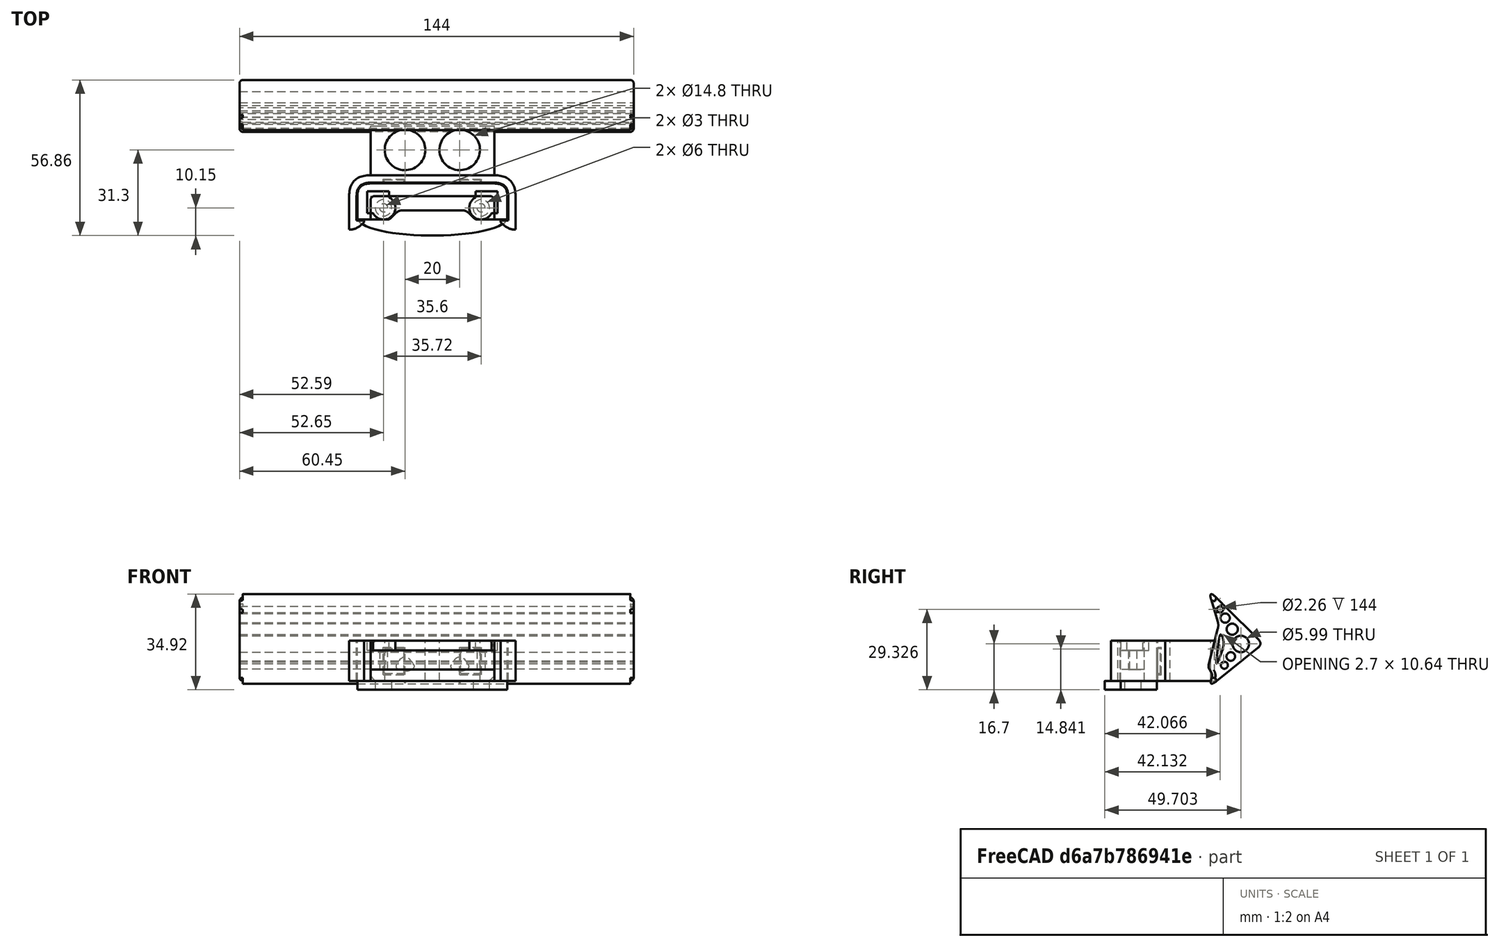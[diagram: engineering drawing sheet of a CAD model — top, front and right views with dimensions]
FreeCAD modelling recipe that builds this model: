
FCSTD DOCUMENT  (FreeCAD 0.19R0.19.2)
Label: 039
License: All rights reserved
LicenseURL: http://en.wikipedia.org/wiki/All_rights_reserved
objects: Sketcher::SketchObject×6, Part::Extrusion×6, Part::Box×5, Part::Cylinder×4, Part::Fillet×3, Part::MultiFuse×2, Part::Cut×2
note: 28 computed .brp shape members not serialized (recipe doc carries the construction recipe); baked Part::Feature solids carry a one-line shape summary decoded from their .brp

FEATURE [Sketcher::SketchObject] Sketch  label="attatchmentPiece"
  FullyConstrained = true
  sketch-geometry (20):
    g0: Circle CenterX=16.25 CenterY=0 CenterZ=0 NormalX=0 NormalY=0 NormalZ=1 AngleXU=0 Radius=1.5
    g1: LineSegment StartX=21.05 StartY=0 StartZ=0 EndX=21.05 EndY=-1 EndZ=0
    g2: LineSegment StartX=21.05 StartY=-1 StartZ=0 EndX=21.05 EndY=-4.3 EndZ=0
    g3: LineSegment StartX=-24.15 StartY=4.3 StartZ=0 EndX=21.05 EndY=4.3 EndZ=0
    g4: LineSegment StartX=21.05 StartY=0 StartZ=0 EndX=21.05 EndY=4.3 EndZ=0
    g5-g8: Circle x4 (B-spline internal-alignment scaffolding for g9; pole/knot coordinates omitted)
    g9: BSplineCurve PolesCount=4 KnotsCount=2 Degree=3 IsPeriodic=0
    g10: GeomPoint X=10.05 Y=-1 Z=0
    g11: GeomPoint X=14.55 Y=-4.3 Z=0
    g12: LineSegment StartX=10.05 StartY=-1 StartZ=0 EndX=-10.05 EndY=-1 EndZ=0
    g13: LineSegment StartX=14.55 StartY=-4.3 StartZ=0 EndX=21.05 EndY=-4.3 EndZ=0
    g14: LineSegment StartX=-24.15 StartY=4.3 StartZ=0 EndX=-24.15 EndY=-4.3 EndZ=0
    g15: LineSegment StartX=-13.15 StartY=-1 StartZ=0 EndX=-10.05 EndY=-1 EndZ=0
    g16: LineSegment StartX=-24.15 StartY=-4.3 StartZ=0 EndX=-19.35 EndY=-4.3 EndZ=0
    g17: Circle CenterX=-19.35 CenterY=0 CenterZ=0 NormalX=0 NormalY=0 NormalZ=1 AngleXU=0 Radius=1.5
    g18: LineSegment StartX=-19.35 StartY=-4.3 StartZ=0 EndX=-17.65 EndY=-4.3 EndZ=0
    g19: BSplineCurve PolesCount=4 KnotsCount=2 Degree=3 IsPeriodic=0
  constraints (41):
    c: Block(g0)
    c: Vertical(g1)
    c: Coincident(g2,g1)
    c: Vertical(g2)
    c: Block(g1)
    c: Horizontal(g3)
    c: Vertical(g4)
    c: Coincident(g4,g3)
    c: Block(g3)
    c: Block(g4)
    c: Weight(g5) = 1
    c: Equal(g5,g6)
    c: Equal(g5,g7)
    c: Equal(g5,g8)
    c: InternalAlignment(g5-g8 -> g9) x4
    c: InternalAlignment(g10,g9)
    c: InternalAlignment(g11,g9)
    c: Block(g9)
    c: Coincident(g12,g9)
    c: Horizontal(g12)
    c: Coincident(g13,g9)
    c: Coincident(g13,g2)
    c: Horizontal(g13)
    c: Distance(g3) = 45.2
    c: Coincident(g14,g3)
    c: Vertical(g14)
    c: Horizontal(g15)
    c: Distance(g15) = 3.1
    c: Block(g17)
    c: Horizontal(g16)
    c: Block(g19)
    c: Coincident(g18,g16)
    c: Coincident(g18,g19)
    c: Horizontal(g18)
    c: Block(g18)
    c: Coincident(g19,g15)
    c: Block(g16)
    c: Block(g12)
    c: Block(g14)
    c: Distance(g16) = 4.8
    c: Distance(g18) = 1.7
FEATURE [Part::Extrusion] Extrude  label="attatchmentPiece001"
  Base = -> Sketch
  Dir = (0,0,1)
  DirMode = 2
  FaceMakerClass = Part::FaceMakerBullseye
  LengthFwd = 7
  LengthRev = 0
  Solid = true
  Symmetric = false
FEATURE [Sketcher::SketchObject] Sketch001  label="attatchmentPieceSurround"
  FullyConstrained = true
  sketch-geometry (18):
    g0: LineSegment StartX=25.85 StartY=-4.3 StartZ=0 EndX=21.05 EndY=-4.3 EndZ=0
    g1: LineSegment StartX=25.85 StartY=-4.3 StartZ=0 EndX=25.85 EndY=4.3 EndZ=0
    g2: LineSegment StartX=-21.05 StartY=8.9 StartZ=0 EndX=21.05 EndY=8.9 EndZ=0
    g3: Circle CenterX=21.05 CenterY=8.9 CenterZ=0 NormalX=0 NormalY=0 NormalZ=1 AngleXU=0 Radius=1
    g4: Circle CenterX=25.85 CenterY=8.9 CenterZ=0 NormalX=0 NormalY=0 NormalZ=1 AngleXU=0 Radius=1
    g5: Circle CenterX=25.85 CenterY=4.3 CenterZ=0 NormalX=0 NormalY=0 NormalZ=1 AngleXU=0 Radius=1
    g6: BSplineCurve PolesCount=3 KnotsCount=2 Degree=2 IsPeriodic=0
    g7: GeomPoint X=21.05 Y=8.9 Z=0
    g8: GeomPoint X=25.85 Y=4.3 Z=0
    g9: ArcOfCircle CenterX=19.45 CenterY=2.7 CenterZ=0 NormalX=0 NormalY=0 NormalZ=1 AngleXU=0 Radius=1.6 StartAngle=0 EndAngle=1.5708
    g10: LineSegment StartX=21.05 StartY=2.7 StartZ=0 EndX=21.05 EndY=-4.3 EndZ=0
    g11: BSplineCurve PolesCount=3 KnotsCount=2 Degree=2 IsPeriodic=0
    g12: LineSegment StartX=-28.95 StartY=-4.3 StartZ=0 EndX=-28.95 EndY=4.3 EndZ=0
    g13: LineSegment StartX=-24.15 StartY=-4.3 StartZ=0 EndX=-28.95 EndY=-4.3 EndZ=0
    g14: LineSegment StartX=-24.15 StartY=2.7 StartZ=0 EndX=-24.15 EndY=-4.3 EndZ=0
    g15: ArcOfCircle CenterX=-22.55 CenterY=2.7 CenterZ=0 NormalX=0 NormalY=0 NormalZ=1 AngleXU=0 Radius=1.6 StartAngle=1.5708 EndAngle=3.14159
    g16: LineSegment StartX=-24.15 StartY=8.9 StartZ=0 EndX=-21.05 EndY=8.9 EndZ=0
    g17: LineSegment StartX=-22.55 StartY=4.3 StartZ=0 EndX=19.45 EndY=4.3 EndZ=0
  constraints (38):
    c: Horizontal(g0)
    c: Vertical(g1)
    c: Coincident(g1,g0)
    c: Horizontal(g2)
    c: Distance(g2) = 42.1
    c: Block(g2)
    c: Coincident(g6,g2)
    c: Weight(g3) = 1
    c: Equal(g3,g4)
    c: Equal(g3,g5)
    c: Coincident(g6,g1)
    c: InternalAlignment(g3,g6)
    c: InternalAlignment(g4,g6)
    c: InternalAlignment(g5,g6)
    c: InternalAlignment(g7,g6)
    c: InternalAlignment(g8,g6)
    c: Block(g0)
    c: Block(g6)
    c: Block(g9)
    c: Coincident(g10,g9)
    c: Coincident(g10,g0)
    c: Vertical(g10)
    c: Horizontal(g13)
    c: Coincident(g12,g13)
    c: Vertical(g12)
    c: Coincident(g11,g12)
    c: Block(g12)
    c: Block(g11)
    c: Block(g15)
    c: Coincident(g14,g15)
    c: Coincident(g14,g13)
    c: Vertical(g14)
    c: Coincident(g16,g11)
    c: Coincident(g16,g2)
    c: Horizontal(g16)
    c: Coincident(g17,g15)
    c: Coincident(g17,g9)
    c: Horizontal(g17)
FEATURE [Part::Extrusion] Extrude001  label="attatchmentPieceSurround001"
  Base = -> Sketch001
  Dir = (0,0,1)
  DirMode = 2
  FaceMakerClass = Part::FaceMakerBullseye
  LengthFwd = 14.7
  LengthRev = 0
  Placement = pos=(0,0,-4.1) rot=(0,0,1;0rad)
  Solid = true
  Symmetric = false
FEATURE [Sketcher::SketchObject] Sketch002  label="attatchmentPieceEndScrewHoleCaps"
  FullyConstrained = true
  sketch-geometry (10):
    g0: ArcOfCircle CenterX=16.25 CenterY=0 CenterZ=0 NormalX=0 NormalY=0 NormalZ=1 AngleXU=0 Radius=4.3 StartAngle=2.05456 EndAngle=5.79942
    g1: LineSegment StartX=14.25 StartY=3.80657 StartZ=0 EndX=14.25 EndY=6 EndZ=0
    g2: LineSegment StartX=20.0566 StartY=-2 StartZ=0 EndX=22.25 EndY=-2 EndZ=0
    g3: LineSegment StartX=22.25 StartY=-2 StartZ=0 EndX=22.25 EndY=6 EndZ=0
    g4: LineSegment StartX=14.25 StartY=6 StartZ=0 EndX=22.25 EndY=6 EndZ=0
    g5: LineSegment StartX=-25.35 StartY=-2 StartZ=0 EndX=-25.35 EndY=6 EndZ=0
    g6: LineSegment StartX=-25.35 StartY=-2 StartZ=0 EndX=-23.1566 EndY=-2 EndZ=0
    g7: LineSegment StartX=-17.35 StartY=6 StartZ=0 EndX=-25.35 EndY=6 EndZ=0
    g8: LineSegment StartX=-17.35 StartY=3.80657 StartZ=0 EndX=-17.35 EndY=6 EndZ=0
    g9: ArcOfCircle CenterX=-19.35 CenterY=0 CenterZ=0 NormalX=0 NormalY=0 NormalZ=1 AngleXU=0 Radius=4.3 StartAngle=3.62536 EndAngle=7.37022
  constraints (25):
    c: Block(g0)
    c: Vertical(g1)
    c: Horizontal(g2)
    c: Coincident(g3,g2)
    c: Vertical(g3)
    c: Coincident(g4,g1)
    c: Horizontal(g4)
    c: Coincident(g3,g4)
    c: Block(g4)
    c: Block(g3)
    c: Coincident(g0,g1)
    c: Coincident(g0,g2)
    c: Block(g1)
    c: Block(g9)
    c: Horizontal(g6)
    c: Vertical(g8)
    c: Coincident(g7,g8)
    c: Horizontal(g7)
    c: Coincident(g5,g6)
    c: Vertical(g5)
    c: Coincident(g5,g7)
    c: Block(g7)
    c: Block(g5)
    c: Coincident(g9,g6)
    c: Coincident(g9,g8)
FEATURE [Part::Extrusion] Extrude002  label="attatchmentPieceEndScrewHoleCaps001"
  Base = -> Sketch002
  Dir = (0,0,1)
  DirMode = 2
  FaceMakerClass = Part::FaceMakerBullseye
  LengthFwd = 3.6
  LengthRev = 0
  Placement = pos=(0,0,7) rot=(0,0,1;0rad)
  Solid = true
  Symmetric = false
FEATURE [Sketcher::SketchObject] Sketch003  label="mainBumpperPieceAttatchment"
  FullyConstrained = true
  sketch-geometry (42):
    g0: Circle CenterX=28.85 CenterY=4.3 CenterZ=0 NormalX=0 NormalY=0 NormalZ=1 AngleXU=0 Radius=1
    g1: Circle CenterX=28.85 CenterY=11.9 CenterZ=0 NormalX=0 NormalY=0 NormalZ=1 AngleXU=0 Radius=1
    g2: Circle CenterX=21.05 CenterY=11.9 CenterZ=0 NormalX=0 NormalY=0 NormalZ=1 AngleXU=0 Radius=1
    g3: BSplineCurve PolesCount=3 KnotsCount=2 Degree=2 IsPeriodic=0
    g4: GeomPoint X=28.85 Y=4.3 Z=0
    g5: GeomPoint X=21.05 Y=11.9 Z=0
    g6: LineSegment StartX=-21.05 StartY=11.9 StartZ=0 EndX=21.05 EndY=11.9 EndZ=0
    g7: LineSegment StartX=28.85 StartY=4.3 StartZ=0 EndX=28.85 EndY=-4.3 EndZ=0
    g8: Circle CenterX=21.05 CenterY=9.2 CenterZ=0 NormalX=0 NormalY=0 NormalZ=1 AngleXU=0 Radius=1
    g9: Circle CenterX=26.15 CenterY=9.2 CenterZ=0 NormalX=0 NormalY=0 NormalZ=1 AngleXU=0 Radius=1
    g10: Circle CenterX=26.15 CenterY=4.3 CenterZ=0 NormalX=0 NormalY=0 NormalZ=1 AngleXU=0 Radius=1
    g11: BSplineCurve PolesCount=3 KnotsCount=2 Degree=2 IsPeriodic=0
    g12: GeomPoint X=21.05 Y=9.2 Z=0
    g13: GeomPoint X=26.15 Y=4.3 Z=0
    g14: LineSegment StartX=-21.05 StartY=9.2 StartZ=0 EndX=21.05 EndY=9.2 EndZ=0
    g15: LineSegment StartX=26.15 StartY=-4.3 StartZ=0 EndX=26.15 EndY=4.3 EndZ=0
    g16: LineSegment StartX=26.15 StartY=-4.3 StartZ=0 EndX=26.15 EndY=-4.6 EndZ=0
    g17: LineSegment StartX=23.45 StartY=-4.6 StartZ=0 EndX=26.15 EndY=-4.6 EndZ=0
    g18: LineSegment StartX=28.85 StartY=-4.3 StartZ=0 EndX=28.85 EndY=-7.9 EndZ=0
    g19: LineSegment StartX=23.45 StartY=-4.6 StartZ=0 EndX=23.45 EndY=-5.3 EndZ=0
    g20: Circle CenterX=28.85 CenterY=-7.9 CenterZ=0 NormalX=0 NormalY=0 NormalZ=1 AngleXU=0 Radius=1
    g21: Circle CenterX=26.15 CenterY=-8.2 CenterZ=0 NormalX=0 NormalY=0 NormalZ=1 AngleXU=0 Radius=1
    g22: Circle CenterX=23.45 CenterY=-5.3 CenterZ=0 NormalX=0 NormalY=0 NormalZ=1 AngleXU=0 Radius=1
    g23: BSplineCurve PolesCount=3 KnotsCount=2 Degree=2 IsPeriodic=0
    g24: GeomPoint X=28.85 Y=-7.9 Z=0
    g25: GeomPoint X=23.45 Y=-5.3 Z=0
    g26: LineSegment StartX=-21.05 StartY=9.2 StartZ=0 EndX=-24.15 EndY=9.2 EndZ=0
    g27: BSplineCurve PolesCount=3 KnotsCount=2 Degree=2 IsPeriodic=0
    g28: LineSegment StartX=-29.25 StartY=-4.3 StartZ=0 EndX=-29.25 EndY=-4.6 EndZ=0
    g29: LineSegment StartX=-29.25 StartY=-4.6 StartZ=0 EndX=-26.55 EndY=-4.6 EndZ=0
    g30: LineSegment StartX=-31.95 StartY=-4.3 StartZ=0 EndX=-31.95 EndY=-7.9 EndZ=0
    g31: LineSegment StartX=-26.55 StartY=-4.6 StartZ=0 EndX=-26.55 EndY=-5.3 EndZ=0
    g32: Circle CenterX=-31.95 CenterY=-7.9 CenterZ=0 NormalX=0 NormalY=0 NormalZ=1 AngleXU=0 Radius=1
    g33: Circle CenterX=-29.25 CenterY=-8.2 CenterZ=0 NormalX=0 NormalY=0 NormalZ=1 AngleXU=0 Radius=1
    g34: Circle CenterX=-26.55 CenterY=-5.3 CenterZ=0 NormalX=0 NormalY=0 NormalZ=1 AngleXU=0 Radius=1
    g35: BSplineCurve PolesCount=3 KnotsCount=2 Degree=2 IsPeriodic=0
    g36: GeomPoint X=-31.95 Y=-7.9 Z=0
    g37: GeomPoint X=-26.55 Y=-5.3 Z=0
    g38: LineSegment StartX=-31.95 StartY=4.3 StartZ=0 EndX=-31.95 EndY=-4.3 EndZ=0
    g39: LineSegment StartX=-29.25 StartY=-4.3 StartZ=0 EndX=-29.25 EndY=4.3 EndZ=0
    g40: BSplineCurve PolesCount=3 KnotsCount=2 Degree=2 IsPeriodic=0
    g41: LineSegment StartX=-21.05 StartY=11.9 StartZ=0 EndX=-24.15 EndY=11.9 EndZ=0
  constraints (78):
    c: Weight(g0) = 1
    c: Equal(g0,g1)
    c: Equal(g0,g2)
    c: InternalAlignment(g0,g3)
    c: InternalAlignment(g1,g3)
    c: InternalAlignment(g2,g3)
    c: InternalAlignment(g4,g3)
    c: InternalAlignment(g5,g3)
    c: Block(g3)
    c: Horizontal(g6)
    c: Vertical(g7)
    c: Block(g7)
    c: Block(g6)
    c: Weight(g8) = 1
    c: Equal(g8,g9)
    c: Equal(g8,g10)
    c: InternalAlignment(g8,g11)
    c: InternalAlignment(g9,g11)
    c: InternalAlignment(g10,g11)
    c: InternalAlignment(g12,g11)
    c: InternalAlignment(g13,g11)
    c: Horizontal(g14)
    c: Vertical(g15)
    c: Block(g11)
    c: Block(g15)
    c: Block(g14)
    c: Coincident(g16,g15)
    c: Vertical(g16)
    c: Distance(g16) = 0.3
    c: Horizontal(g17)
    c: Coincident(g17,g16)
    c: Coincident(g18,g7)
    c: Vertical(g18)
    c: Distance(g18) = 3.6
    c: Vertical(g19)
    c: Coincident(g19,g17)
    c: Coincident(g23,g18)
    c: Weight(g20) = 1
    c: Equal(g20,g21)
    c: Equal(g20,g22)
    c: Coincident(g23,g19)
    c: InternalAlignment(g20,g23)
    c: InternalAlignment(g21,g23)
    c: InternalAlignment(g22,g23)
    c: InternalAlignment(g24,g23)
    c: InternalAlignment(g25,g23)
    c: Block(g23)
    c: Horizontal(g26)
    c: Distance(g26) = 3.1
    c: Block(g27)
    c: Vertical(g38)
    c: Block(g38)
    c: Vertical(g39)
    c: Block(g40)
    c: Block(g39)
    c: Vertical(g28)
    c: Coincident(g28,g39)
    c: Coincident(g29,g28)
    c: Horizontal(g29)
    c: Vertical(g30)
    c: Coincident(g30,g38)
    c: Coincident(g31,g29)
    c: Vertical(g31)
    c: Coincident(g35,g30)
    c: Equal(g32,g33)
    c: Equal(g32,g34)
    c: Coincident(g35,g31)
    c: InternalAlignment(g32,g35)
    c: InternalAlignment(g33,g35)
    c: InternalAlignment(g34,g35)
    c: InternalAlignment(g36,g35)
    c: InternalAlignment(g37,g35)
    c: Block(g35)
    c: Coincident(g40,g26)
    c: Block(g29)
    c: Horizontal(g41)
    c: Equal(g26,g41) = 3.1
    c: Coincident(g41,g6)
FEATURE [Part::Box] Box  label="bumpperExtension"
  AttacherType = Attacher::AttachEngine3D
  Height = 14.7
  Length = 45.2
  Placement = pos=(-24.15,11.9,-4.1) rot=(0,0,1;0rad)
  Width = 18
FEATURE [Sketcher::SketchObject] Sketch004  label="bumpperMain"
  FullyConstrained = true
  Placement = pos=(0,0,0) rot=(0.57735,0.57735,0.57735;2.0944rad)
  sketch-geometry (62):
    g0: Circle CenterX=-3.12329 CenterY=2.49901 CenterZ=0 NormalX=0 NormalY=0 NormalZ=1 AngleXU=0 Radius=1
    g1: Circle CenterX=0 CenterY=0 CenterZ=0 NormalX=0 NormalY=0 NormalZ=1 AngleXU=0 Radius=1
    g2: Circle CenterX=-1.35243 CenterY=3.60648 CenterZ=0 NormalX=0 NormalY=0 NormalZ=1 AngleXU=0 Radius=1
    g3: BSplineCurve PolesCount=3 KnotsCount=2 Degree=2 IsPeriodic=0
    g4: GeomPoint X=-3.12329 Y=2.49901 Z=0
    g5: GeomPoint X=-1.35243 Y=3.60648 Z=0
    g6: Circle CenterX=-2.83953 CenterY=33.0261 CenterZ=0 NormalX=0 NormalY=0 NormalZ=1 AngleXU=0 Radius=1
    g7: Circle CenterX=0 CenterY=35.8434 CenterZ=0 NormalX=0 NormalY=0 NormalZ=1 AngleXU=0 Radius=1
    g8: Circle CenterX=-1.15771 CenterY=32.0146 CenterZ=0 NormalX=0 NormalY=0 NormalZ=1 AngleXU=0 Radius=1
    g9: BSplineCurve PolesCount=3 KnotsCount=2 Degree=2 IsPeriodic=0
    g10: GeomPoint X=-2.83953 Y=33.0261 Z=0
    g11: GeomPoint X=-1.15771 Y=32.0146 Z=0
    g12: Circle CenterX=-18.2963 CenterY=17.6904 CenterZ=0 NormalX=0 NormalY=0 NormalZ=1 AngleXU=0 Radius=1
    g13: Circle CenterX=-20 CenterY=16 CenterZ=0 NormalX=0 NormalY=0 NormalZ=1 AngleXU=0 Radius=1
    g14: Circle CenterX=-18.1259 CenterY=14.5008 CenterZ=0 NormalX=0 NormalY=0 NormalZ=1 AngleXU=0 Radius=1
    g15: BSplineCurve PolesCount=3 KnotsCount=2 Degree=2 IsPeriodic=0
    g16: GeomPoint X=-18.2963 Y=17.6904 Z=0
    g17: GeomPoint X=-18.1259 Y=14.5008 Z=0
    g18: LineSegment StartX=-18.2963 StartY=17.6904 StartZ=0 EndX=-2.83953 EndY=33.0261 EndZ=0
    g19: LineSegment StartX=-18.1259 StartY=14.5008 StartZ=0 EndX=-3.12329 EndY=2.49901 EndZ=0
    g20: Circle CenterX=-11.9527 CenterY=16 CenterZ=0 NormalX=0 NormalY=0 NormalZ=1 AngleXU=0 Radius=2.99582
    g21: Circle CenterX=-8.803 CenterY=21.3731 CenterZ=0 NormalX=0 NormalY=0 NormalZ=1 AngleXU=0 Radius=2.03939
    g22: Circle CenterX=-6.23123 CenterY=25.4475 CenterZ=0 NormalX=0 NormalY=0 NormalZ=1 AngleXU=0 Radius=1.69309
    g23: Circle CenterX=-4.38186 CenterY=28.6261 CenterZ=0 NormalX=0 NormalY=0 NormalZ=1 AngleXU=0 Radius=1.13029
    g24: Circle CenterX=-8.28033 CenterY=11.4296 CenterZ=0 NormalX=0 NormalY=0 NormalZ=1 AngleXU=0 Radius=1.57213
    g25: Circle CenterX=-5.93972 CenterY=8.22213 CenterZ=0 NormalX=0 NormalY=0 NormalZ=1 AngleXU=0 Radius=1.28743
    g26: Circle CenterX=-3.47023 CenterY=24.3665 CenterZ=0 NormalX=0 NormalY=0 NormalZ=1 AngleXU=0 Radius=1
    g27: Circle CenterX=-3.90437 CenterY=22.9307 CenterZ=0 NormalX=0 NormalY=0 NormalZ=1 AngleXU=0 Radius=1
    g28: Circle CenterX=-3.53772 CenterY=21.4762 CenterZ=0 NormalX=0 NormalY=0 NormalZ=1 AngleXU=0 Radius=1
    g29: BSplineCurve PolesCount=3 KnotsCount=2 Degree=2 IsPeriodic=0
    g30: GeomPoint X=-3.47023 Y=24.3665 Z=0
    g31: GeomPoint X=-3.53772 Y=21.4762 Z=0
    g32: LineSegment StartX=-1.15771 StartY=32.0146 StartZ=0 EndX=-3.47023 EndY=24.3665 EndZ=0
    g33: Circle CenterX=-5.41867 CenterY=17.9226 CenterZ=0 NormalX=0 NormalY=0 NormalZ=1 AngleXU=0 Radius=1
    g34: Circle CenterX=-6 CenterY=16 CenterZ=0 NormalX=0 NormalY=0 NormalZ=1 AngleXU=0 Radius=1
    g35: Circle CenterX=-5.22753 CenterY=13.9401 CenterZ=0 NormalX=0 NormalY=0 NormalZ=1 AngleXU=0 Radius=1
    g36: BSplineCurve PolesCount=3 KnotsCount=2 Degree=2 IsPeriodic=0
    g37: GeomPoint X=-5.41867 Y=17.9226 Z=0
    g38: GeomPoint X=-5.22753 Y=13.9401 Z=0
    g39: Circle CenterX=-3.98946 CenterY=10.6386 CenterZ=0 NormalX=0 NormalY=0 NormalZ=1 AngleXU=0 Radius=1
    g40: Circle CenterX=-2.58497 CenterY=6.89324 CenterZ=0 NormalX=0 NormalY=0 NormalZ=1 AngleXU=0 Radius=1
    g41: Circle CenterX=-3.11001 CenterY=10.8586 CenterZ=0 NormalX=0 NormalY=0 NormalZ=1 AngleXU=0 Radius=1
    g42: BSplineCurve PolesCount=3 KnotsCount=2 Degree=2 IsPeriodic=0
    g43: GeomPoint X=-3.98946 Y=10.6386 Z=0
    g44: GeomPoint X=-3.11001 Y=10.8586 Z=0
    g45: Circle CenterX=-1.35243 CenterY=3.60648 CenterZ=0 NormalX=0 NormalY=0 NormalZ=1 AngleXU=0 Radius=1
    g46: Circle CenterX=-1.76142 CenterY=4.69712 CenterZ=0 NormalX=0 NormalY=0 NormalZ=1 AngleXU=0 Radius=1
    g47: Circle CenterX=-1.05937 CenterY=5.79125 CenterZ=0 NormalX=0 NormalY=0 NormalZ=1 AngleXU=0 Radius=1
    g48: BSplineCurve PolesCount=3 KnotsCount=2 Degree=2 IsPeriodic=0
    g49: GeomPoint X=-1.35243 Y=3.60648 Z=0
    g50: GeomPoint X=-1.05937 Y=5.79125 Z=0
    g51: Circle CenterX=-0.519336 CenterY=6.6329 CenterZ=0 NormalX=0 NormalY=0 NormalZ=1 AngleXU=0 Radius=1
    g52: Circle CenterX=0 CenterY=7.44228 CenterZ=0 NormalX=0 NormalY=0 NormalZ=1 AngleXU=0 Radius=1
    g53: Circle CenterX=-0.244436 CenterY=8.41194 CenterZ=0 NormalX=0 NormalY=0 NormalZ=1 AngleXU=0 Radius=1
    g54: BSplineCurve PolesCount=3 KnotsCount=2 Degree=2 IsPeriodic=0
    g55: GeomPoint X=-0.519336 Y=6.6329 Z=0
    g56: GeomPoint X=-0.244436 Y=8.41194 Z=0
    g57: LineSegment StartX=-3.53772 StartY=21.4762 StartZ=0 EndX=-0.244436 EndY=8.41194 EndZ=0
    g58: LineSegment StartX=-5.22753 StartY=13.9401 StartZ=0 EndX=-3.98946 EndY=10.6386 EndZ=0
    g59: LineSegment StartX=-1.05937 StartY=5.79125 StartZ=0 EndX=-0.519336 EndY=6.6329 EndZ=0
    g60: BSplineCurve PolesCount=3 KnotsCount=2 Degree=2 IsPeriodic=0
    g61: LineSegment StartX=-4.0304 StartY=17.8099 StartZ=0 EndX=-3.11001 EndY=10.8586 EndZ=0
  constraints (96):
    c: Weight(g0) = 1
    c: Equal(g0,g1)
    c: Equal(g0,g2)
    c: InternalAlignment(g0,g3)
    c: InternalAlignment(g1,g3)
    c: InternalAlignment(g2,g3)
    c: InternalAlignment(g4,g3)
    c: InternalAlignment(g5,g3)
    c: Block(g3)
    c: Weight(g6) = 1
    c: Equal(g6,g7)
    c: Equal(g6,g8)
    c: InternalAlignment(g6,g9)
    c: InternalAlignment(g7,g9)
    c: InternalAlignment(g8,g9)
    c: InternalAlignment(g10,g9)
    c: InternalAlignment(g11,g9)
    c: Block(g9)
    c: Weight(g12) = 1
    c: Equal(g12,g13)
    c: Equal(g12,g14)
    c: InternalAlignment(g12,g15)
    c: InternalAlignment(g13,g15)
    c: InternalAlignment(g14,g15)
    c: InternalAlignment(g16,g15)
    c: InternalAlignment(g17,g15)
    c: Block(g15)
    c: Coincident(g18,g15)
    c: Coincident(g18,g9)
    c: Coincident(g19,g15)
    c: Coincident(g19,g3)
    c: Block(g25)
    c: Block(g24)
    c: Block(g20)
    c: Block(g21)
    c: Block(g22)
    c: Block(g23)
    c: Weight(g26) = 1
    c: Equal(g26,g27)
    c: Equal(g26,g28)
    c: InternalAlignment(g26,g29)
    c: InternalAlignment(g27,g29)
    c: InternalAlignment(g28,g29)
    c: InternalAlignment(g30,g29)
    c: InternalAlignment(g31,g29)
    c: Block(g29)
    c: Coincident(g32,g9)
    c: Coincident(g32,g29)
    c: Weight(g33) = 1
    c: Equal(g33,g34)
    c: Equal(g33,g35)
    c: InternalAlignment(g33,g36)
    c: InternalAlignment(g34,g36)
    c: InternalAlignment(g35,g36)
    c: InternalAlignment(g37,g36)
    c: InternalAlignment(g38,g36)
    c: Block(g36)
    c: Weight(g39) = 1
    c: Equal(g39,g40)
    c: Equal(g39,g41)
    c: InternalAlignment(g39,g42)
    c: InternalAlignment(g40,g42)
    c: InternalAlignment(g41,g42)
    c: InternalAlignment(g43,g42)
    c: InternalAlignment(g44,g42)
    c: Block(g42)
    c: Coincident(g48,g3)
    c: Weight(g45) = 1
    c: Equal(g45,g46)
    c: Equal(g45,g47)
    c: InternalAlignment(g45,g48)
    c: InternalAlignment(g46,g48)
    c: InternalAlignment(g47,g48)
    c: InternalAlignment(g49,g48)
    c: InternalAlignment(g50,g48)
    c: Block(g48)
    c: Weight(g51) = 1
    c: Equal(g51,g52)
    c: Equal(g51,g53)
    c: InternalAlignment(g51,g54)
    c: InternalAlignment(g52,g54)
    c: InternalAlignment(g53,g54)
    c: InternalAlignment(g55,g54)
    c: InternalAlignment(g56,g54)
    c: Block(g54)
    c: Coincident(g57,g29)
    c: Coincident(g57,g54)
    c: Block(g57)
    c: Coincident(g58,g36)
    c: Coincident(g58,g42)
    c: Coincident(g59,g48)
    c: Coincident(g59,g54)
    c: Block(g60)
    c: Coincident(g60,g36)
    c: Coincident(g61,g60)
    c: Coincident(g61,g42)
FEATURE [Part::Extrusion] Extrude004  label="bumpperMain001"
  Base = -> Sketch004
  Dir = (1,0,0)
  DirMode = 2
  FaceMakerClass = Part::FaceMakerBullseye
  LengthFwd = 144
  LengthRev = 0
  Placement = pos=(72,27.6,-6.6) rot=(0,0,1;3.14159rad)
  Solid = true
  Symmetric = false
FEATURE [Sketcher::SketchObject] Sketch005  label="attatchmentPieceBottom"
  FullyConstrained = true
  sketch-geometry (20):
    g0: LineSegment StartX=25.85 StartY=-4.3 StartZ=0 EndX=25.85 EndY=4.3 EndZ=0
    g1: LineSegment StartX=-21.05 StartY=8.9 StartZ=0 EndX=21.05 EndY=8.9 EndZ=0
    g2: Circle CenterX=21.05 CenterY=8.9 CenterZ=0 NormalX=0 NormalY=0 NormalZ=1 AngleXU=0 Radius=1
    g3: Circle CenterX=25.85 CenterY=8.9 CenterZ=0 NormalX=0 NormalY=0 NormalZ=1 AngleXU=0 Radius=1
    g4: Circle CenterX=25.85 CenterY=4.3 CenterZ=0 NormalX=0 NormalY=0 NormalZ=1 AngleXU=0 Radius=1
    g5: BSplineCurve PolesCount=3 KnotsCount=2 Degree=2 IsPeriodic=0
    g6: GeomPoint X=21.05 Y=8.9 Z=0
    g7: GeomPoint X=25.85 Y=4.3 Z=0
    g8: BSplineCurve PolesCount=3 KnotsCount=2 Degree=2 IsPeriodic=0
    g9: LineSegment StartX=-28.95 StartY=-4.3 StartZ=0 EndX=-28.95 EndY=4.3 EndZ=0
    g10: LineSegment StartX=-24.15 StartY=8.9 StartZ=0 EndX=-21.05 EndY=8.9 EndZ=0
    g11: Circle CenterX=-19.41 CenterY=0 CenterZ=0 NormalX=0 NormalY=0 NormalZ=1 AngleXU=0 Radius=3
    g12: Circle CenterX=16.3103 CenterY=0 CenterZ=0 NormalX=0 NormalY=0 NormalZ=1 AngleXU=0 Radius=3
    g13-g16: Circle x4 (B-spline internal-alignment scaffolding for g17; pole/knot coordinates omitted)
    g17: BSplineCurve PolesCount=4 KnotsCount=2 Degree=3 IsPeriodic=0
    g18: GeomPoint X=-28.95 Y=-4.3 Z=0
    g19: GeomPoint X=25.85 Y=-4.3 Z=0
  constraints (36):
    c: Vertical(g0)
    c: Horizontal(g1)
    c: Distance(g1) = 42.1
    c: Block(g1)
    c: Coincident(g5,g1)
    c: Weight(g2) = 1
    c: Equal(g2,g3)
    c: Equal(g2,g4)
    c: Coincident(g5,g0)
    c: InternalAlignment(g2,g5)
    c: InternalAlignment(g3,g5)
    c: InternalAlignment(g4,g5)
    c: InternalAlignment(g6,g5)
    c: InternalAlignment(g7,g5)
    c: Block(g5)
    c: Vertical(g9)
    c: Coincident(g8,g9)
    c: Block(g9)
    c: Block(g8)
    c: Coincident(g10,g8)
    c: Coincident(g10,g1)
    c: Horizontal(g10)
    c: PointOnObject(g12,g-1)
    c: PointOnObject(g11,g-1)
    c: Block(g11)
    c: Block(g12)
    c: Coincident(g17,g9)
    c: Weight(g13) = 1
    c: Equal(g13,g14)
    c: Equal(g13,g15)
    c: Equal(g13,g16)
    c: Coincident(g17,g0)
    c: InternalAlignment(g13-g16 -> g17) x4
    c: InternalAlignment(g18,g17)
    c: InternalAlignment(g19,g17)
    c: Block(g17)
FEATURE [Part::Extrusion] Extrude005  label="attatchmentPieceBottom001"
  Base = -> Sketch005
  Dir = (0,0,1)
  DirMode = 2
  FaceMakerClass = Part::FaceMakerBullseye
  LengthFwd = 3.2
  LengthRev = 0
  Placement = pos=(0,0,-7.3) rot=(0,0,1;0rad)
  Solid = true
  Symmetric = false
FEATURE [Part::Extrusion] Extrude006  label="mainBumpperPieceAttatchment001"
  Base = -> Sketch003
  Dir = (0,0,1)
  DirMode = 2
  FaceMakerClass = Part::FaceMakerBullseye
  LengthFwd = 14.7
  LengthRev = 0
  Placement = pos=(0,0,-4.1) rot=(0,0,1;0rad)
  Solid = true
  Symmetric = false
FEATURE [Part::Cylinder] Cylinder  label="removeFromBumpperExtension"
  Angle = 360
  AttacherType = Attacher::AttachEngine3D
  Height = 20
  Placement = pos=(8.45,21.15,-8) rot=(0,0,1;0rad)
  Radius = 7.4
FEATURE [Part::Cylinder] Cylinder001  label="removeFromBumpperExtension001"
  Angle = 360
  AttacherType = Attacher::AttachEngine3D
  Height = 20
  Placement = pos=(-11.55,21.15,-8) rot=(0,0,1;0rad)
  Radius = 7.4
FEATURE [Part::MultiFuse] Fusion  label="removeFromBumpperExtension002"
  Shapes = -> [Cylinder,Cylinder001]
FEATURE [Part::Cylinder] Cylinder002  label="removeFromBumpperExtension004"
  Angle = 360
  AttacherType = Attacher::AttachEngine3D
  Height = 20
  Placement = pos=(8.45,21.15,-8) rot=(0,0,1;0rad)
  Radius = 7.4
FEATURE [Part::Cylinder] Cylinder003  label="removeFromBumpperExtension005"
  Angle = 360
  AttacherType = Attacher::AttachEngine3D
  Height = 20
  Placement = pos=(-11.55,21.15,-8) rot=(0,0,1;0rad)
  Radius = 7.4
FEATURE [Part::MultiFuse] Fusion001  label="removeFromBumpperMain"
  Shapes = -> [Cylinder002,Cylinder003]
FEATURE [Part::Cut] Cut  label="bumpperExtension001"
  Base = -> Box
  Tool = -> Fusion
FEATURE [Part::Cut] Cut001  label="bumpperMain002"
  Base = -> Extrude004
  Tool = -> Fusion001
FEATURE [Part::Fillet] Fillet  label="bumpperExtension002"
  Base = -> Cut
  Edges = 4 edges r=3: [Edge2,Edge4,Edge9,Edge14]
FEATURE [Part::Fillet] Fillet001
  Base = -> Cut001
  Edges = 11 edges r=1.2: [Edge4,Edge7,Edge10,Edge30,Edge31,Edge32,Edge33,Edge34,Edge35,Edge36,Edge37]
FEATURE [Part::Fillet] Fillet002  label="bumpperMain003"
  Base = -> Fillet001
  Edges = 11 edges r=1.2: [Edge4,Edge9,Edge13,Edge14,Edge15,Edge16,Edge17,Edge18,Edge19,Edge20,Edge21]
FEATURE [Part::Box] Box001  label="bumpperExtensionBumpHole"
  AttacherType = Attacher::AttachEngine3D
  Height = 10
  Length = 8
  Placement = pos=(8.45,9.2,-1.8) rot=(0,0,1;0rad)
  Width = 1.3
FEATURE [Part::Box] Box002  label="bumpperExtensionBumpHole001"
  AttacherType = Attacher::AttachEngine3D
  Height = 10
  Length = 8
  Placement = pos=(-19.55,9.2,-1.8) rot=(0,0,1;0rad)
  Width = 1.3
FEATURE [Part::Box] Box003  label="attatchmentPieceSurroundBump"
  AttacherType = Attacher::AttachEngine3D
  Height = 9.2
  Length = 7.2
  Placement = pos=(8.85,8.9,-1.4) rot=(0,0,1;0rad)
  Width = 1.3
FEATURE [Part::Box] Box004  label="attatchmentPieceSurroundBump001"
  AttacherType = Attacher::AttachEngine3D
  Height = 9.2
  Length = 7.2
  Placement = pos=(-19.15,8.9,-1.4) rot=(0,0,1;0rad)
  Width = 1.3
